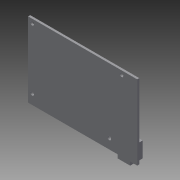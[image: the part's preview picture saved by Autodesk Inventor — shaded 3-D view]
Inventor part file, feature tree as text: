
AUTODESK INVENTOR PART (.ipt)
format: ipt  version: 2013 (Build 170138000, 138)  size: 114,688 bytes
history: native  units: mm
features: extrude x2, sketch x2
ambient origin geometry x8: Origin, YZ Plane, XZ Plane, XY Plane, X Axis, Y Axis, Z Axis, Center Point
bodies: Solid1 (feature_tree)
feature tree (4):
  extrude  "Extrusion1"  Depth=5.08mm
  extrude  "Extrusion2"  Depth=66.04mm
  sketch  "Sketch1"  dims[d1=3.8mm d2=5.08mm]
  sketch  "Sketch2"  dims[d3=100.076mm d4=66.04mm d5=22.86mm d6=4.318mm d7=3.5mm d8=96.266mm d9=4.318mm d10=3.5mm d11=62.23mm d12=11.176mm d13=3.5mm d14=3.5mm d15=10.922mm d16=11.938mm d17=2.0mm d18=0.0mm d20=11.938mm d21=6.0mm d22=12.0mm d23=12.0mm d24=0.0mm d25=5.4mm]
